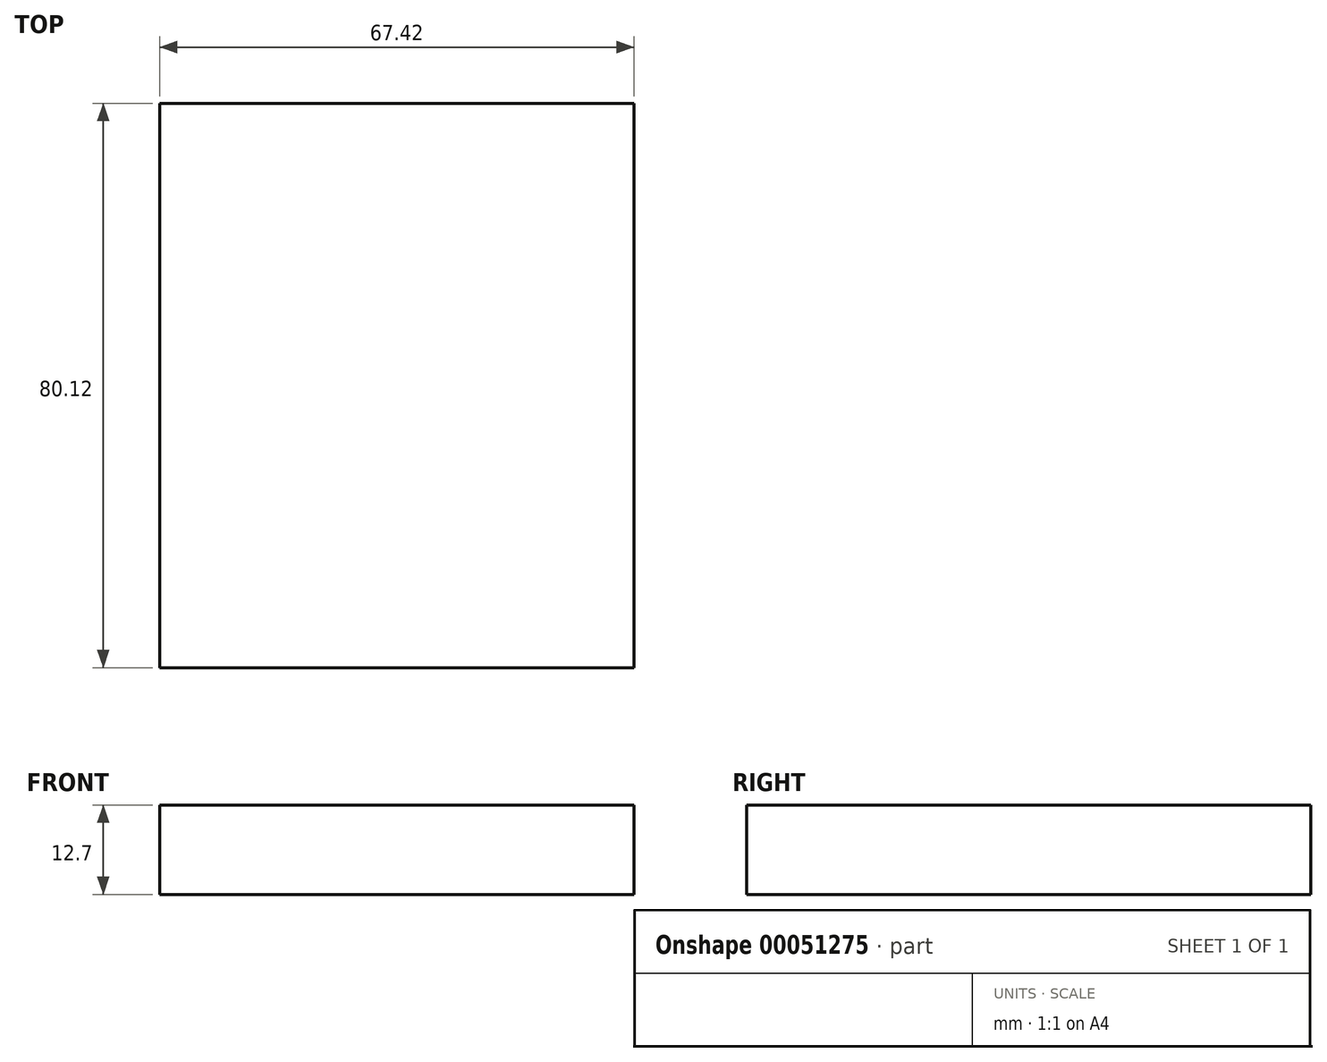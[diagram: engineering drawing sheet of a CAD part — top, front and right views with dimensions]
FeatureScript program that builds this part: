
annotation { "Feature Type Name" : "Feature", "Feature Type Description" : "" }
export const myFeature = defineFeature(function(context is Context, id is Id, definition is map)
    precondition{}
    {
        {
            var Q0;
            Q0=qCreatedBy(makeId("Top.planeOp"),FACE);
            var sketch = newSketch(context, id + "F0", { "sketchPlane" : qUnion([Q0])});
            skLineSegment(sketch, "E0.bottom", {"start": v(-37.52, -30.08) * mm, "end": v(29.9, -30.08) * mm});
            skLineSegment(sketch, "E0.top", {"start": v(-37.52, 50.04) * mm, "end": v(29.9, 50.04) * mm});
            skLineSegment(sketch, "E0.left", {"start": v(-37.52, -30.08) * mm, "end": v(-37.52, 50.04) * mm});
            skLineSegment(sketch, "E0.right", {"start": v(29.9, -30.08) * mm, "end": v(29.9, 50.04) * mm});
            skSolve(sketch);
        }
        {
            var Q0;
            Q0=makeQuery(id+"F0.imprint","IMPRINT",FACE,{"disambiguationData":[TD([[makeQuery(id+"F0.imprint","IMPRINT",EDGE,{"derivedFrom":sQuery(id+"F0.wireOp",EDGE,"E0.bottom")}),1.0]])]});
            extrude(context, id + "F1", {"entities" : qUnion([Q0]), "depth" : 12.7 * mm});
        }
    });
